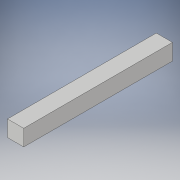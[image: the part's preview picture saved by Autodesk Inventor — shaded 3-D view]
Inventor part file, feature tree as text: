
AUTODESK INVENTOR PART (.ipt)
format: ipt  version: 2019 (Build 230136000, 136)  size: 91,136 bytes
history: native  units: in
note: dims shown in document units (in); Inventor stores cm internally (conversion verified against a paired STEP export)
features: extrude x1, sketch x1
ambient origin geometry x8: Origin, YZ Plane, XZ Plane, XY Plane, X Axis, Y Axis, Z Axis, Center Point
bodies: Solid1 (feature_tree)
feature tree (2):
  extrude  "Extrusion1"  Depth=0.125in
  sketch  "Sketch1"  dims[d0=0.125in d1=0.125in d2=1.15in d3=0.0in]
